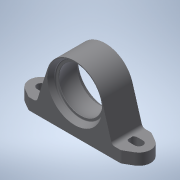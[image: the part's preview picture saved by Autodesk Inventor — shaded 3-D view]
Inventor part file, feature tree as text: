
AUTODESK INVENTOR PART (.ipt)
format: ipt  version: 2022.1 (Build 261234000, 234)  size: 226,816 bytes
history: native  units: mm (DEFAULTED — no unit token found)
features: sketch x5, extrude x4, revolve x1
ambient origin geometry x8: Origin, YZ Plane, XZ Plane, XY Plane, X Axis, Y Axis, Z Axis, Center Point
bodies: Solid1 (feature_tree)
feature tree (10):
  revolve  "Revolution1"  [1 undecoded]
  extrude  "Extrusion1"  Depth=42.9mm TaperAngle=0.0deg
  extrude  "Extrusion2"  Depth=238.5mm
  extrude  "Extrusion4"  Depth=11.0mm
  extrude  "Extrusion5"  Depth=11.0mm
  sketch  "Sketch_1"  dims[d0=360.0deg d1=40.0mm d2=0.0mm]
  sketch  "Sketch_2"  dims[d3=42.9mm d4=0.0mm d9=42.9mm d10=0.0mm]
  sketch  "Sketch_3"  dims[d11=42.9mm d12=0.0mm d30=238.5mm]
  sketch  "Sketch_8"  dims[d32=7.0mm d33=11.0mm]
  sketch  "Sketch_10"  dims[d34=57.0mm d35=11.0mm d36=7.0mm d37=57.0mm d38=25.1mm d39=37.1mm d40=5.0mm d41=5.0mm d43=10.1mm d44=49.0mm d45=10.1mm d46=10.0mm]
note: 1 required parameter value undecoded (feature->parameter linkage not recoverable at this tier; creation-order binding heuristic only, values carry confidence <= 0.55)
